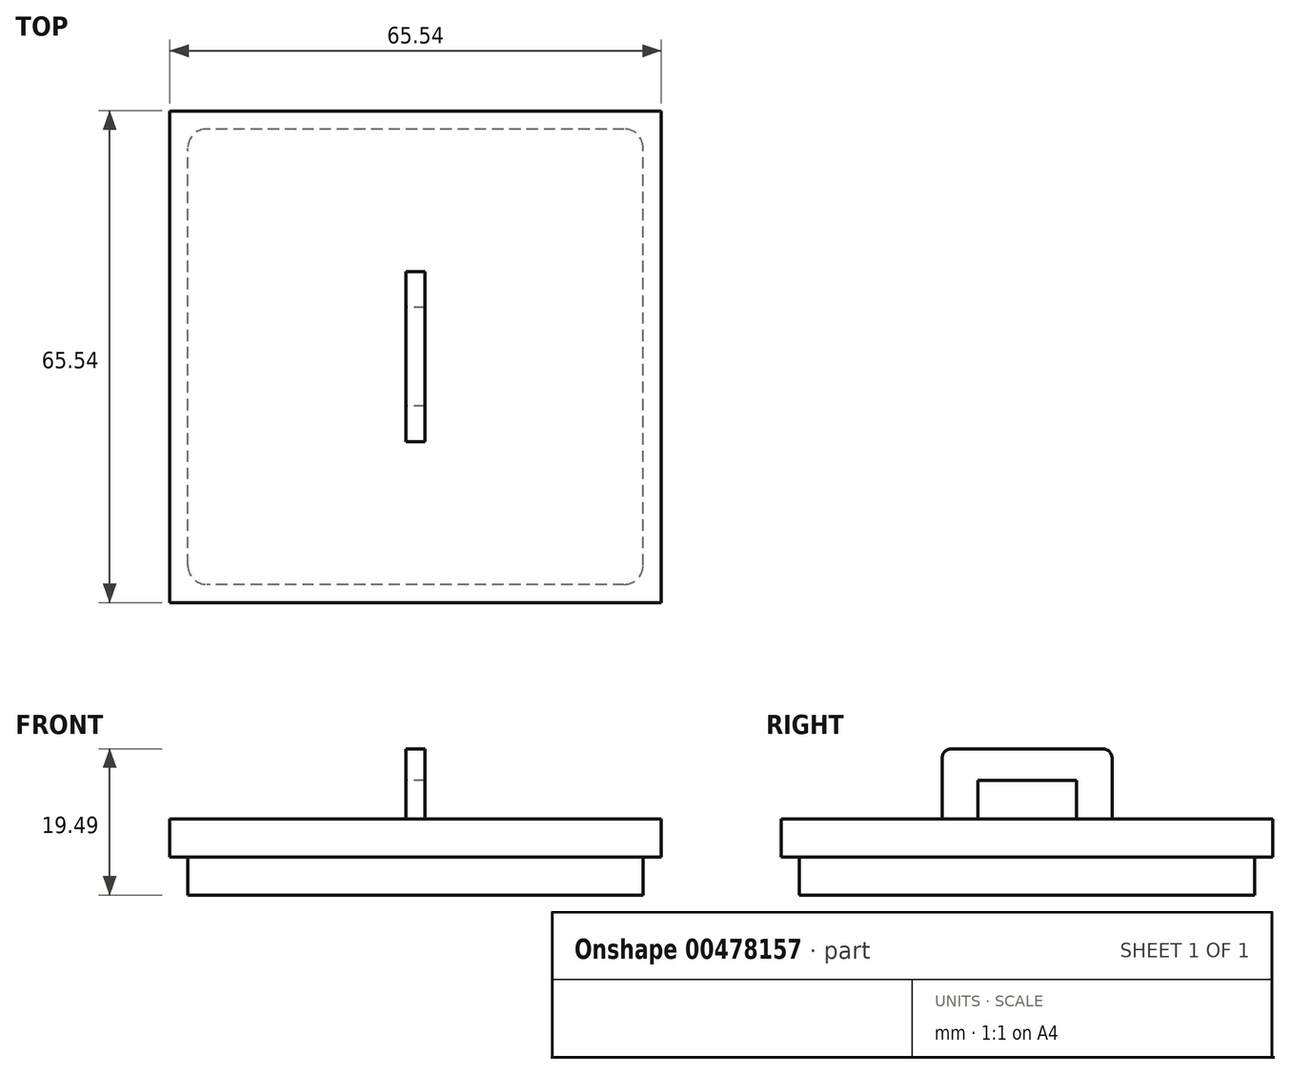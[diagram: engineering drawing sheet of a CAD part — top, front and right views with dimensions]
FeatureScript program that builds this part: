
annotation { "Feature Type Name" : "Feature", "Feature Type Description" : "" }
export const myFeature = defineFeature(function(context is Context, id is Id, definition is map)
    precondition{}
    {
        {
            var Q0;
            Q0=qCreatedBy(makeId("Top.planeOp"),FACE);
            var sketch = newSketch(context, id + "F0", { "sketchPlane" : qUnion([Q0])});
            skLineSegment(sketch, "E0.bottom", {"start": v(32.77, 32.77) * mm, "end": v(-32.77, 32.77) * mm});
            skLineSegment(sketch, "E0.top", {"start": v(32.77, -32.77) * mm, "end": v(-32.77, -32.77) * mm});
            skLineSegment(sketch, "E0.left", {"start": v(32.77, 32.77) * mm, "end": v(32.77, -32.77) * mm});
            skLineSegment(sketch, "E0.right", {"start": v(-32.77, 32.77) * mm, "end": v(-32.77, -32.77) * mm});
            skPoint(sketch, "E0.middle", {"position": v(0, 0) * mm});
            skSolve(sketch);
        }
        {
            var Q0;
            Q0 = qSketchRegion(id + "F0", true);
            extrude(context, id + "F1", {"entities" : qUnion([Q0]), "oppositeDirection" : true, "depth" : 5.08 * mm, "offsetDistance" : 25.4 * mm});
        }
        {
            var Q0;
            Q0=qCreatedBy(makeId("Top.planeOp"),FACE);
            var sketch = newSketch(context, id + "F2", { "sketchPlane" : qUnion([Q0])});
            skLineSegment(sketch, "E1.bottom", {"start": v(30.35, -30.35) * mm, "end": v(-30.35, -30.35) * mm});
            skLineSegment(sketch, "E1.top", {"start": v(30.35, 30.35) * mm, "end": v(-30.35, 30.35) * mm});
            skLineSegment(sketch, "E1.left", {"start": v(30.35, -30.35) * mm, "end": v(30.35, 30.35) * mm});
            skLineSegment(sketch, "E1.right", {"start": v(-30.35, -30.35) * mm, "end": v(-30.35, 30.35) * mm});
            skPoint(sketch, "E1.middle", {"position": v(0, 0) * mm});
            skSolve(sketch);
        }
        {
            var Q0;
            Q0 = qSketchRegion(id + "F2", true);
            extrude(context, id + "F3", {"entities" : qUnion([Q0]), "operationType" : NewBodyOperationType.ADD, "oppositeDirection" : true, "depth" : 10.16 * mm, "offsetDistance" : 25.4 * mm});
        }
        {
            var Q0;
            Q0=makeQuery(id+"F3.opExtrude","SWEPT_EDGE",EDGE,{"disambiguationData":[OSD([sQuery(id+"F2.wireOp",EDGE,"E1.top"),sQuery(id+"F2.wireOp",EDGE,"E1.right")])]});
            var Q1;
            Q1=makeQuery(id+"F3.opExtrude","SWEPT_EDGE",EDGE,{"disambiguationData":[OSD([sQuery(id+"F2.wireOp",EDGE,"E1.top"),sQuery(id+"F2.wireOp",EDGE,"E1.left")])]});
            var Q2;
            Q2=makeQuery(id+"F3.opExtrude","SWEPT_EDGE",EDGE,{"disambiguationData":[OSD([sQuery(id+"F2.wireOp",EDGE,"E1.bottom"),sQuery(id+"F2.wireOp",EDGE,"E1.left")])]});
            var Q3;
            Q3=makeQuery(id+"F3.opExtrude","SWEPT_EDGE",EDGE,{"disambiguationData":[OSD([sQuery(id+"F2.wireOp",EDGE,"E1.bottom"),sQuery(id+"F2.wireOp",EDGE,"E1.right")])]});
            fillet(context, id + "F4", {"entities" : qUnion([Q0, Q1, Q2, Q3]), "radius" : 2.54 * mm, "tangentPropagation" : true, "allowEdgeOverflow" : false});
        }
        {
            var Q0;
            Q0=qCreatedBy(makeId("Right.planeOp"),FACE);
            var sketch = newSketch(context, id + "F5", { "sketchPlane" : qUnion([Q0])});
            skLineSegment(sketch, "E2", {"start": v(-11.34, 0) * mm, "end": v(-11.34, 9.33) * mm});
            skLineSegment(sketch, "E3", {"start": v(-11.34, 9.33) * mm, "end": v(11.34, 9.33) * mm});
            skLineSegment(sketch, "E4", {"start": v(11.34, 9.33) * mm, "end": v(11.34, 0) * mm});
            skLineSegment(sketch, "E5", {"start": v(11.34, 0) * mm, "end": v(6.58, 0) * mm});
            skLineSegment(sketch, "E6", {"start": v(6.58, 0) * mm, "end": v(6.58, 5.12) * mm});
            skLineSegment(sketch, "E7", {"start": v(6.58, 5.12) * mm, "end": v(-6.58, 5.12) * mm});
            skLineSegment(sketch, "E8", {"start": v(-6.58, 5.12) * mm, "end": v(-6.58, 0) * mm});
            skLineSegment(sketch, "E9", {"start": v(-6.58, 0) * mm, "end": v(-11.34, 0) * mm});
            skLineSegment(sketch, "E10", {"start": v(0, 0) * mm, "end": v(0, 49.58) * mm});
            skSolve(sketch);
        }
        {
            var Q0;
            Q0 = qSketchRegion(id + "F5", true);
            extrude(context, id + "F6", {"entities" : qUnion([Q0]), "operationType" : NewBodyOperationType.ADD, "depth" : 1.27 * mm, "offsetDistance" : 25.4 * mm});
        }
        {
            var Q0;
            Q0=makeQuery(id+"F1.opExtrude","SWEPT_BODY",BODY,{"disambiguationData":[OSD([sQuery(id+"F0.wireOp",EDGE,"E0.bottom"),sQuery(id+"F0.wireOp",EDGE,"E0.top"),sQuery(id+"F0.wireOp",EDGE,"E0.left"),sQuery(id+"F0.wireOp",EDGE,"E0.right")])]});
            var Q1;
            Q1=qCreatedBy(makeId("Right.planeOp"),FACE);
            mirror(context, id + "F7", {"operationType" : NewBodyOperationType.ADD, "entities" : qUnion([Q0]), "mirrorPlane" : qUnion([Q1])});
        }
        {
            var Q0;
            {var subQ0=makeQuery(id+"F6.opExtrude","SWEPT_EDGE",EDGE,{"disambiguationData":[OSD([sQuery(id+"F5.wireOp",EDGE,"E2"),sQuery(id+"F5.wireOp",EDGE,"E3")])]});Q0=makeQuery(id+"F7.boolean.opBoolean","MERGE",EDGE,{"derivedFrom":[subQ0,makeQuery(id+"F7.opPattern","COPY",EDGE,{"derivedFrom":subQ0,"instanceName":"1"})]});}
            var Q1;
            {var subQ0=makeQuery(id+"F6.opExtrude","SWEPT_EDGE",EDGE,{"disambiguationData":[OSD([sQuery(id+"F5.wireOp",EDGE,"E3"),sQuery(id+"F5.wireOp",EDGE,"E4")])]});Q1=makeQuery(id+"F7.boolean.opBoolean","MERGE",EDGE,{"derivedFrom":[subQ0,makeQuery(id+"F7.opPattern","COPY",EDGE,{"derivedFrom":subQ0,"instanceName":"1"})]});}
            fillet(context, id + "F8", {"entities" : qUnion([Q0, Q1]), "radius" : 1.27 * mm, "tangentPropagation" : true, "allowEdgeOverflow" : false});
        }
    });
